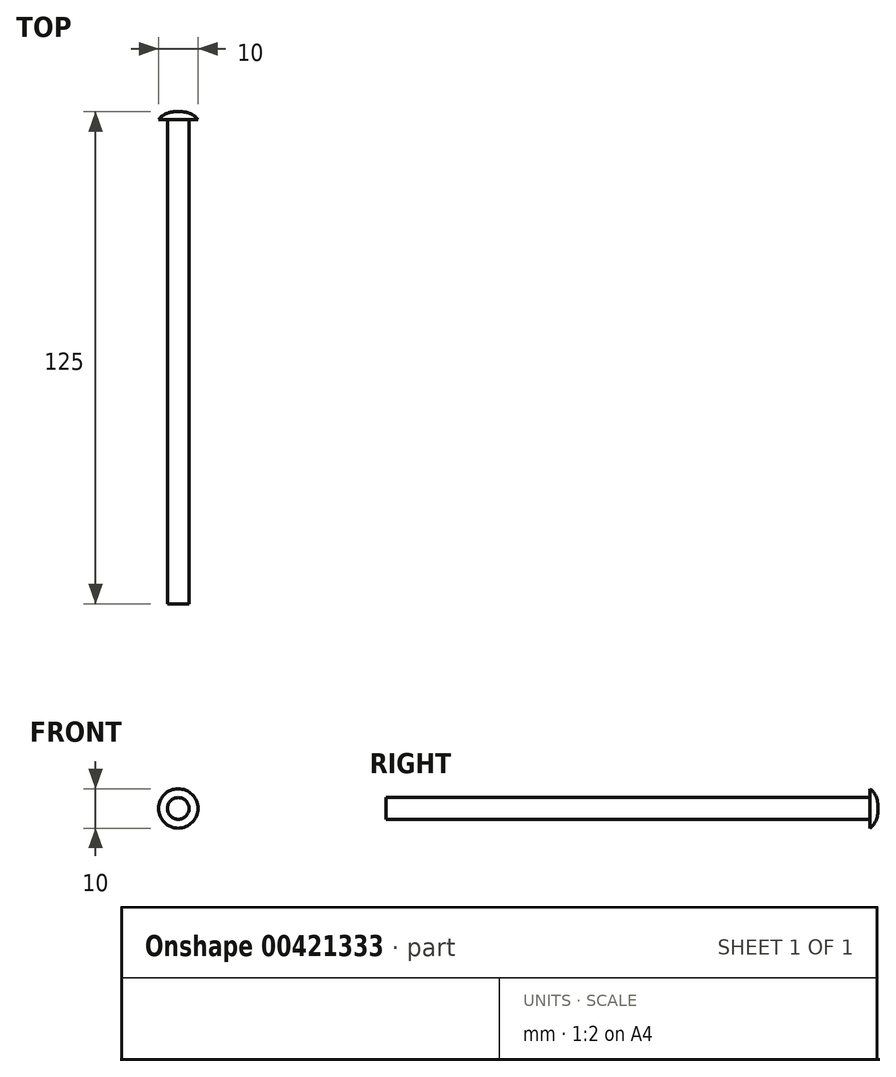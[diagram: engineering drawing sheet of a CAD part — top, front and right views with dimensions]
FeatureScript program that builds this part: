
annotation { "Feature Type Name" : "Feature", "Feature Type Description" : "" }
export const myFeature = defineFeature(function(context is Context, id is Id, definition is map)
    precondition{}
    {
        {
            var Q0;
            Q0=qCreatedBy(makeId("Front.planeOp"),FACE);
            var sketch = newSketch(context, id + "F0", { "sketchPlane" : qUnion([Q0])});
            skCircle(sketch, "E0", {"center": v(0, 0) * mm, "radius": 2.75 * mm});
            skSolve(sketch);
        }
        {
            var Q0;
            Q0=makeQuery(id+"F0.imprint","IMPRINT",FACE,{"disambiguationData":[TD([[makeQuery(id+"F0.imprint","IMPRINT",EDGE,{"derivedFrom":sQuery(id+"F0.wireOp",EDGE,"E0")}),1.0]])]});
            extrude(context, id + "F1", {"entities" : qUnion([Q0]), "depth" : 125 * mm});
        }
        {
            var Q0;
            Q0=qCreatedBy(makeId("Front.planeOp"),FACE);
            var sketch = newSketch(context, id + "F2", { "sketchPlane" : qUnion([Q0])});
            skCircle(sketch, "E1", {"center": v(0, 0) * mm, "radius": 5 * mm});
            skSolve(sketch);
        }
        {
            var Q0;
            Q0 = qSketchRegion(id + "F2", true);
            extrude(context, id + "F3", {"entities" : qUnion([Q0]), "operationType" : NewBodyOperationType.ADD, "depth" : 2 * mm});
        }
        {
            var Q0;
            Q0=makeQuery(id+"F3.opExtrude","CAP_EDGE",EDGE,{"disambiguationData":[OSD([sQuery(id+"F2.wireOp",EDGE,"E1")])],"isStart":true});
            fillet(context, id + "F4", {"entities" : qUnion([Q0]), "radius" : 5 * mm, "tangentPropagation" : true, "allowEdgeOverflow" : false});
        }
    });
